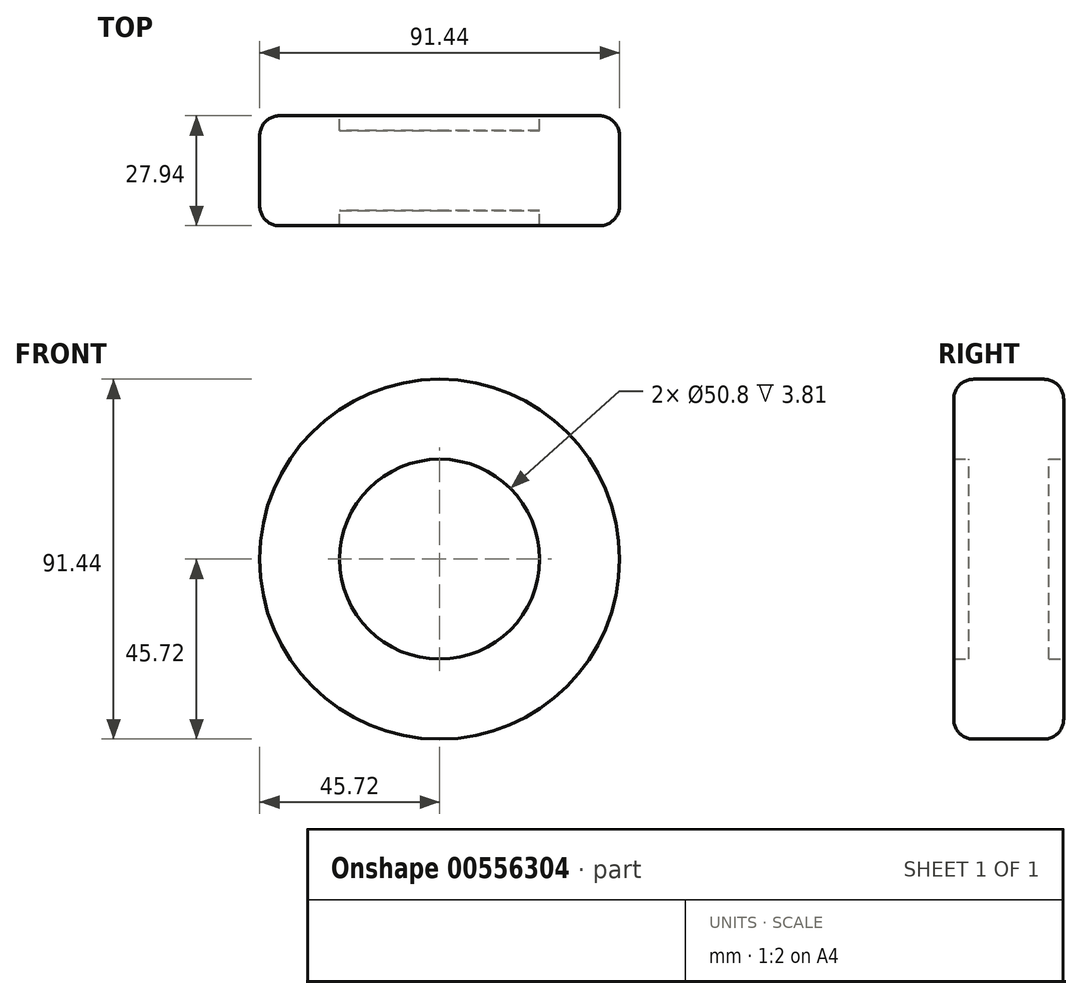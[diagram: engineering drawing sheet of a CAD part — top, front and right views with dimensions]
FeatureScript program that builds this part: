
annotation { "Feature Type Name" : "Feature", "Feature Type Description" : "" }
export const myFeature = defineFeature(function(context is Context, id is Id, definition is map)
    precondition{}
    {
        {
            var Q0;
            Q0=qCreatedBy(makeId("Front.planeOp"),FACE);
            var sketch = newSketch(context, id + "F0", { "sketchPlane" : qUnion([Q0])});
            skCircle(sketch, "E0", {"center": v(0, 0) * mm, "radius": 25.4 * mm});
            skSolve(sketch);
        }
        {
            var Q0;
            Q0=makeQuery(id+"F0.imprint","IMPRINT",FACE,{"disambiguationData":[TD([[makeQuery(id+"F0.imprint","IMPRINT",EDGE,{"derivedFrom":sQuery(id+"F0.wireOp",EDGE,"E0")}),1.0]])]});
            var Q1;
            Q1=sQuery(id+"F0.wireOp",EDGE,"E0");
            extrude(context, id + "F1", {"entities" : qUnion([Q0]), "surfaceEntities" : qUnion([Q1]), "endBound" : BoundingType.SYMMETRIC, "depth" : 20.32 * mm, "offsetDistance" : 25.4 * mm});
        }
        {
            var Q0;
            Q0=qCreatedBy(makeId("Front.planeOp"),FACE);
            var sketch = newSketch(context, id + "F2", { "sketchPlane" : qUnion([Q0])});
            skCircle(sketch, "E1", {"center": v(0, 0) * mm, "radius": 25.4 * mm});
            skCircle(sketch, "E2", {"center": v(0, 0) * mm, "radius": 45.72 * mm});
            skSolve(sketch);
        }
        {
            var Q0;
            Q0 = qSketchRegion(id + "F2", true);
            extrude(context, id + "F3", {"entities" : qUnion([Q0]), "operationType" : NewBodyOperationType.ADD, "endBound" : BoundingType.SYMMETRIC, "depth" : 27.94 * mm, "offsetDistance" : 25.4 * mm});
        }
        {
            var Q0;
            Q0=makeQuery(id+"F3.opExtrude","CAP_EDGE",EDGE,{"disambiguationData":[OSD([sQuery(id+"F2.wireOp",EDGE,"E2")])],"isStart":true});
            var Q1;
            Q1=makeQuery(id+"F3.opExtrude","CAP_EDGE",EDGE,{"disambiguationData":[OSD([sQuery(id+"F2.wireOp",EDGE,"E2")])],"isStart":false});
            fillet(context, id + "F4", {"entities" : qUnion([Q0, Q1]), "radius" : 5.08 * mm, "tangentPropagation" : true, "allowEdgeOverflow" : false});
        }
    });
